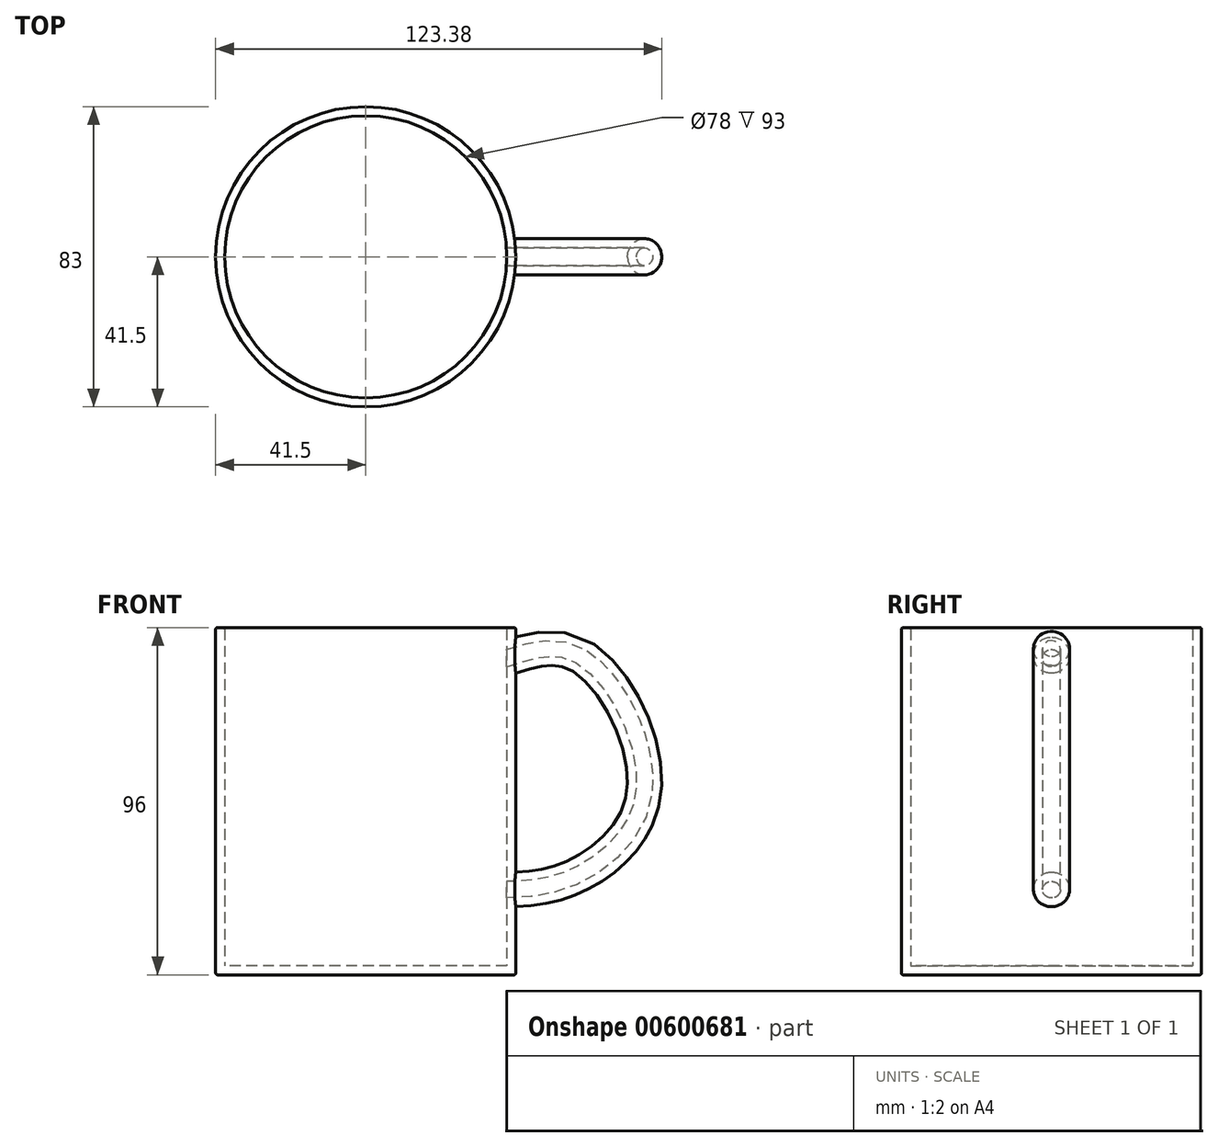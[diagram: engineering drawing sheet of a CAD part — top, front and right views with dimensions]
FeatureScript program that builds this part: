
annotation { "Feature Type Name" : "Feature", "Feature Type Description" : "" }
export const myFeature = defineFeature(function(context is Context, id is Id, definition is map)
    precondition{}
    {
        {
            var Q0;
            Q0=qCreatedBy(makeId("Top.planeOp"),FACE);
            var sketch = newSketch(context, id + "F0", { "sketchPlane" : qUnion([Q0])});
            skCircle(sketch, "E0", {"center": v(0, 0) * mm, "radius": 41.5 * mm});
            skSolve(sketch);
        }
        {
            var Q0;
            Q0=makeQuery(id+"F0.imprint","IMPRINT",FACE,{"disambiguationData":[TD([[makeQuery(id+"F0.imprint","IMPRINT",EDGE,{"derivedFrom":sQuery(id+"F0.wireOp",EDGE,"E0")}),1.0]])]});
            extrude(context, id + "F1", {"entities" : qUnion([Q0]), "depth" : 96 * mm, "offsetDistance" : 25 * mm});
        }
        {
            var Q0;
            Q0=qCreatedBy(makeId("Front.planeOp"),FACE);
            var sketch = newSketch(context, id + "F2", { "sketchPlane" : qUnion([Q0])});
            skFitSpline(sketch, "E1", {"points": [v(33, 88.03) * mm, v(60.51, 90.33) * mm, v(79.37, 49.56) * mm, v(56.95, 24.08) * mm, v(34.02, 21.02) * mm], "startDerivative": vector(121.5, 46.1) * mm, "endDerivative": vector(-104.5, 1.27) * mm});
            skSolve(sketch);
        }
        {
            var Q0;
            Q0=qCreatedBy(makeId("Right.planeOp"),FACE);
            cPlane(context, id + "F3", {"entities" : qUnion([Q0]), "cplaneType" : CPlaneType.OFFSET, "offset" : 41.5 * mm, "width" : 150 * mm, "height" : 150 * mm});
        }
        {
            var Q0;
            Q0=qCreatedBy(id+"F3.planeOp",FACE);
            var sketch = newSketch(context, id + "F4", { "sketchPlane" : qUnion([Q0])});
            skCircle(sketch, "E2", {"center": v(0, 88.36) * mm, "radius": 5 * mm});
            skSolve(sketch);
        }
        {
            var Q0;
            Q0=makeQuery(id+"F4.imprint","IMPRINT",FACE,{"disambiguationData":[TD([[makeQuery(id+"F4.imprint","IMPRINT",EDGE,{"derivedFrom":sQuery(id+"F4.wireOp",EDGE,"E2")}),1.0]])]});
            var Q1;
            Q1=sQuery(id+"F2.wireOp",EDGE,"E1");
            sweep(context, id + "F5", {"operationType" : NewBodyOperationType.ADD, "profiles" : qUnion([Q0]), "path" : qUnion([Q1])});
        }
        {
            var Q0;
            Q0=makeQuery(id+"F1.opExtrude","CAP_FACE",FACE,{"disambiguationData":[OSD([sQuery(id+"F0.wireOp",EDGE,"E0")])],"isStart":false});
            shell(context, id + "F6", {"entities" : qUnion([Q0]), "thickness" : 2.5 * mm});
        }
        {
            var Q0;
            Q0=makeQuery(id+"F1.opExtrude","CAP_FACE",FACE,{"disambiguationData":[OSD([sQuery(id+"F0.wireOp",EDGE,"E0")])],"isStart":false});
            var Q1;
            Q1=makeQuery(id+"F1.opExtrude","CAP_EDGE",EDGE,{"disambiguationData":[OSD([sQuery(id+"F0.wireOp",EDGE,"E0")])],"isStart":true});
            fillet(context, id + "F7", {"entities" : qUnion([Q0, Q1]), "radius" : 0.5 * mm, "tangentPropagation" : true, "allowEdgeOverflow" : false});
        }
    });
